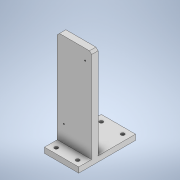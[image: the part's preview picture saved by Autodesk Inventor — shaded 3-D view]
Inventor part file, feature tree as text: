
AUTODESK INVENTOR PART (.ipt)
format: ipt  version: 2020 (Build 240168000, 168)  size: 247,808 bytes
history: native  units: mm
features: sketch x8, extrude x7, hole x4, chamfer x1
ambient origin geometry x8: Origin, YZ Plane, XZ Plane, XY Plane, X Axis, Y Axis, Z Axis, Center Point
bodies: Solid1 (feature_tree)
feature tree (20):
  extrude  "Extrusion1"  TaperAngle=45.0deg  [1 undecoded]
  sketch  "Sketch5"  dims[d35=0.0mm d36=5.0mm]
  extrude  "Extrusion3"  Depth=5.0mm
  extrude  "Extrusion4"  TaperAngle=45.0deg  [1 undecoded]
  hole  "Hole3"  [1 undecoded]
  hole  "Hole4"  [1 undecoded]
  chamfer  "Chamfer1"  Distance=3.0mm
  hole  "Hole5"  [1 undecoded]
  extrude  "Extrusion6"  Depth=6.0mm
  extrude  "Extrusion7"  Depth=6.0mm
  hole  "Hole6"  [1 undecoded]
  extrude  "Extrusion8"  TaperAngle=0.0deg  [1 undecoded]
  extrude  "Extrusion9"  Depth=2.0mm TaperAngle=45.0deg
  sketch  "Sketch1"  dims[d3=0.0mm d33=45.0deg]
  sketch  "Sketch6"  dims[d37=5.0mm d38=45.0deg]
  sketch  "Sketch7"  dims[d39=9.999938mm d42=0.0mm]
  sketch  "Sketch8"  dims[d43=5.0mm d44=2.0mm]
  sketch  "Sketch10"  dims[d45=2.0mm]
  sketch  "Sketch12"  dims[d46=2.0mm]
  sketch  "Sketch14"  dims[d47=2.0mm d48=3.0mm d49=0.0mm d52=0.0mm d53=4.496mm d54=6.0mm d55=7.938mm d56=4.166mm d57=14.3117mm d58=8.0mm d59=20.594885mm d60=6.0mm d61=6.0mm d62=6.0mm d63=0.0mm d64=45.0deg d65=0.0mm d66=5.0mm d67=5.0mm d68=45.0deg d69=9.999938mm d70=0.0mm d71=5.0mm d72=2.0mm d73=2.0mm d74=2.0mm d75=2.0mm d76=2.4mm d77=4.0mm d78=4.4mm d79=2.0mm d80=90.0deg d81=5.0mm d82=20.594885mm d83=2.0mm d84=2.0mm d85=45.0deg d90=9.912mm d91=9.912mm d92=3.5mm d93=3.5mm d94=4.496mm d95=4.0mm d96=8.433mm d97=2.0mm d98=14.3117mm d99=5.0mm d100=20.594885mm d103=18.0mm d104=0.0mm d105=5.0mm d106=0.0mm d107=32.0mm d109=3.302mm d110=8.0mm d111=4.0mm d112=2.0mm d113=90.0deg d114=8.0mm d115=0.0mm d116=10.0mm d117=10.0mm d118=32.0mm d119=32.0mm d120=10.0mm d121=10.0mm d122=20.0mm d123=10.0mm d124=10.0mm d125=35.0mm d127=6.0mm d128=18.0mm d129=10.0mm d130=0.0mm d131=2.0mm d132=3.0mm d133=0.0mm]
note: 7 required parameter values undecoded (feature->parameter linkage not recoverable at this tier; creation-order binding heuristic only, values carry confidence <= 0.55)
